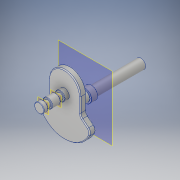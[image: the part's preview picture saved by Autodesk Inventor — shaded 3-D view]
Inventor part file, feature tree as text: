
AUTODESK INVENTOR PART (.ipt)
format: ipt  version: 2018 (Build 220112000, 112)  size: 239,616 bytes
history: native  units: in
note: dims shown in document units (in); Inventor stores cm internally (conversion verified against a paired STEP export)
features: sketch x7, extrude x6, fillet x4, plane x3, chamfer x1, hole x1, thread x1
ambient origin geometry x8: Origin, YZ Plane, XZ Plane, XY Plane, X Axis, Y Axis, Z Axis, Center Point
bodies: Solid1 (feature_tree)
feature tree (23):
  extrude  "Extrusion1"  Depth=0.2in
  fillet  "Fillet1"  Radius=0.073in
  fillet  "Fillet2"  Radius=0.0625in
  extrude  "Extrusion2"  Depth=0.3055in TaperAngle=0.0deg
  plane  "Work Plane1"
  extrude  "Extrusion3"  Depth=0.078in
  plane  "Work Plane2"
  extrude  "Extrusion4"  [1 undecoded]
  chamfer  "Chamfer1"  Distance=0.05in
  extrude  "Extrusion5"  Depth=0.1155in
  hole  "Hole1"  [1 undecoded]
  thread  "Thread1"  [1 undecoded]
  plane  "Work Plane3"
  extrude  "Extrusion6"  Depth=0.0025in
  fillet  "Fillet3"  Radius=0.075in
  fillet  "Fillet4"  Radius=0.0025in
  sketch  "Sketch1"  dims[d6=0.2in d7=0.2in d10=0.073in d11=0.0in d12=0.0625in]
  sketch  "Sketch2"  dims[d13=0.01in d15=0.3055in d16=0.0in]
  sketch  "Sketch3"  dims[d17=-0.05in d18=0.078in]
  sketch  "Sketch4"  dims[d19=0.05in d20=0.0in d21=-0.1in d22=0.05in d23=0.0in]
  sketch  "Sketch5"  dims[d24=0.005in d25=0.125in d26=45.0deg d27=0.1155in]
  sketch  "Sketch6"  dims[d28=0.92in d29=0.0in]
  sketch  "Sketch7"  dims[d30=0.075in d31=0.75in d32=0.1in d33=0.25in d34=45.0deg d35=0.158in d36=0.8108in d37=1.0in d38=0.0in d39=0.175in d40=0.1555in d41=0.075in d42=0.0in d43=0.0025in d44=0.0025in]
note: 3 required parameter values undecoded (feature->parameter linkage not recoverable at this tier; creation-order binding heuristic only, values carry confidence <= 0.55)
